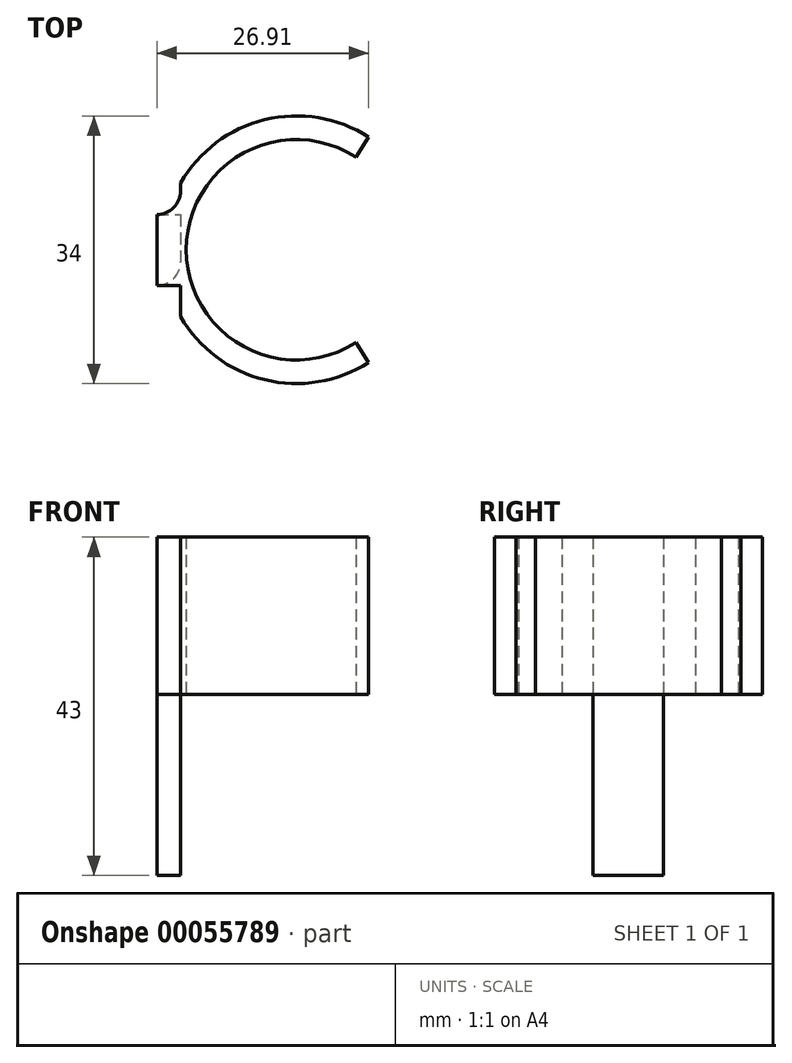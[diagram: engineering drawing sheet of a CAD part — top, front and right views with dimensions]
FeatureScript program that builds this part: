
annotation { "Feature Type Name" : "Feature", "Feature Type Description" : "" }
export const myFeature = defineFeature(function(context is Context, id is Id, definition is map)
    precondition{}
    {
        {
            var Q0;
            Q0=qCreatedBy(makeId("Top.planeOp"),FACE);
            var sketch = newSketch(context, id + "F0", { "sketchPlane" : qUnion([Q0])});
            skArc(sketch, "E0", {"start": v(9.17, 14.31) * mm, "mid": v(-4.03, 16.52) * mm, "end": v(-14.74, 8.48) * mm});
            skArc(sketch, "E1.0", {"start": v(7.55, 11.79) * mm, "mid": v(-14, 0) * mm, "end": v(7.55, -11.79) * mm});
            skLineSegment(sketch, "E2", {"start": v(7.55, 11.79) * mm, "end": v(9.17, 14.31) * mm});
            skLineSegment(sketch, "E3", {"start": v(7.55, -11.79) * mm, "end": v(9.17, -14.31) * mm});
            skLineSegment(sketch, "E4", {"start": v(-14.74, 8.48) * mm, "end": v(-14.74, -8.48) * mm});
            skArc(sketch, "E5.trimOffspring", {"start": v(-14.74, -8.48) * mm, "mid": v(-4.03, -16.52) * mm, "end": v(9.17, -14.31) * mm});
            skSolve(sketch);
        }
        {
            var Q0;
            Q0 = qSketchRegion(id + "F0", true);
            extrude(context, id + "F1", {"entities" : qUnion([Q0]), "depth" : 20 * mm});
        }
        {
            var Q0;
            Q0=makeQuery(id+"F1.opExtrude","SWEPT_FACE",FACE,{"disambiguationData":[OSD([sQuery(id+"F0.wireOp",EDGE,"E4")])]});
            var sketch = newSketch(context, id + "F2", { "sketchPlane" : qUnion([Q0])});
            skLineSegment(sketch, "E6.top", {"start": v(-4.47, -23) * mm, "end": v(4.53, -23) * mm});
            skLineSegment(sketch, "E6.left", {"start": v(-4.47, 20) * mm, "end": v(-4.47, -23) * mm});
            skLineSegment(sketch, "E6.right", {"start": v(4.53, 20) * mm, "end": v(4.53, -23) * mm});
            skPoint(sketch, "E7.end.orphan", {"position": v(4.53, 16) * mm});
            skLineSegment(sketch, "E8", {"start": v(-4.47, 20) * mm, "end": v(4.53, 20) * mm});
            skSolve(sketch);
        }
        {
            var Q0;
            Q0 = qSketchRegion(id + "F2", true);
            extrude(context, id + "F3", {"entities" : qUnion([Q0]), "operationType" : NewBodyOperationType.ADD, "depth" : 3 * mm});
        }
        {
            var Q0;
            Q0 = qSketchRegion(id + "F2", true);
            extrude(context, id + "F4", {"entities" : qUnion([Q0]), "operationType" : NewBodyOperationType.ADD, "depth" : 3 * mm});
        }
        {
            var Q0;
            {var subQ0=sQuery(id+"F2.wireOp",EDGE,"E6.left");var subQ1=sQuery(id+"F2.wireOp",EDGE,"E6.bottom");Q0=makeQuery(id+"F3.boolean.opBoolean","SPLIT",EDGE,{"disambiguationData":[TD([makeQuery(id+"F3.opExtrude","SWEPT_FACE",FACE,{"disambiguationData":[OSD([subQ1])]})])],"derivedFrom":makeQuery(id+"F3.opExtrude","CAP_EDGE",EDGE,{"disambiguationData":[OSD([subQ0])],"isStart":true})});}
            var Q1;
            {var subQ0=sQuery(id+"F2.wireOp",EDGE,"E6.right");var subQ1=sQuery(id+"F2.wireOp",EDGE,"E6.bottom");Q1=makeQuery(id+"F3.boolean.opBoolean","SPLIT",EDGE,{"disambiguationData":[TD([makeQuery(id+"F3.opExtrude","SWEPT_FACE",FACE,{"disambiguationData":[OSD([subQ1])]})])],"derivedFrom":makeQuery(id+"F3.opExtrude","CAP_EDGE",EDGE,{"disambiguationData":[OSD([subQ0])],"isStart":true})});}
            var Q2;
            {var subQ0=sQuery(id+"F2.wireOp",EDGE,"E6.left");Q2=makeQuery(id+"F3.boolean.opBoolean","SPLIT",EDGE,{"disambiguationData":[topologyDisambiguationEdgeConnected([makeQuery(id+"F1.opExtrude","SWEPT_FACE",FACE,{"disambiguationData":[OSD([sQuery(id+"F0.wireOp",EDGE,"E4")])]})])],"derivedFrom":makeQuery(id+"F3.opExtrude","CAP_EDGE",EDGE,{"disambiguationData":[OSD([subQ0])],"isStart":true})});}
            var Q3;
            {var subQ0=sQuery(id+"F2.wireOp",EDGE,"E6.right");Q3=makeQuery(id+"F3.boolean.opBoolean","SPLIT",EDGE,{"disambiguationData":[topologyDisambiguationEdgeConnected([makeQuery(id+"F1.opExtrude","SWEPT_FACE",FACE,{"disambiguationData":[OSD([sQuery(id+"F0.wireOp",EDGE,"E4")])]})])],"derivedFrom":makeQuery(id+"F3.opExtrude","CAP_EDGE",EDGE,{"disambiguationData":[OSD([subQ0])],"isStart":true})});}
            fillet(context, id + "F5", {"entities" : qUnion([Q0, Q1, Q2, Q3]), "radius" : 3 * mm, "tangentPropagation" : true, "allowEdgeOverflow" : false});
        }
    });
